# Revit family: Dental_Equipment-Midmark-Sterilizer_M11-05X
name_source: partatom
category: Specialty Equipment
units: mm (PartAtom-declared; Revit-internal decimal feet)

## family parameters
Always vertical = Yes
Cut with Voids When Loaded = No
OmniClass Number = 23.40.70.11.14.11
OmniClass Title = Medical Equipment
Part Type = Normal
Room Calculation Point = No
Round Connector Dimension = Use Diameter
Shared = No
Work Plane-Based = No

## types (2) — shared parameters
Chamber = 27.9 cm dia. x 45.7 cm deep (11 in dia. x 18 in deep)
Description = Midmark® Steam Sterilizers
Heat Emission = 5275 kJ (5000 BTU)/ hr during operation
Height = 47.2 cm
Length = 59.7 cm
Manufacturer = Midmark
Min Support Surface = 55.4 cm x 67.3 cm (21.8 in x 26.5 in)
Model = M11
Number of Poles = 1
Power Factor = 1
Product Page URL = https://www.midmark.com
Product data url = https://bimobject.com
URL = https://www.midmark.com
Version = 1
Water Reservoir Capacity = 5.3 liters (1.4 gallons) to Full Mark
Weight = 99.00 lbf
Width = 45.2 cm
zero-valued in all types: Default Elevation

## per-type parameters (varying)
| type | Connector Description | Pouch Rack |
| M11-050 | 115 V/50 – 60 Hz/12 A |  |
| M11-051 | 230 V/50 – 60 Hz/6.4 A | 6 slot |

## geometry (parser evidence)
native form markers: Sweep x2
no freeform markers — native parametric forms only
